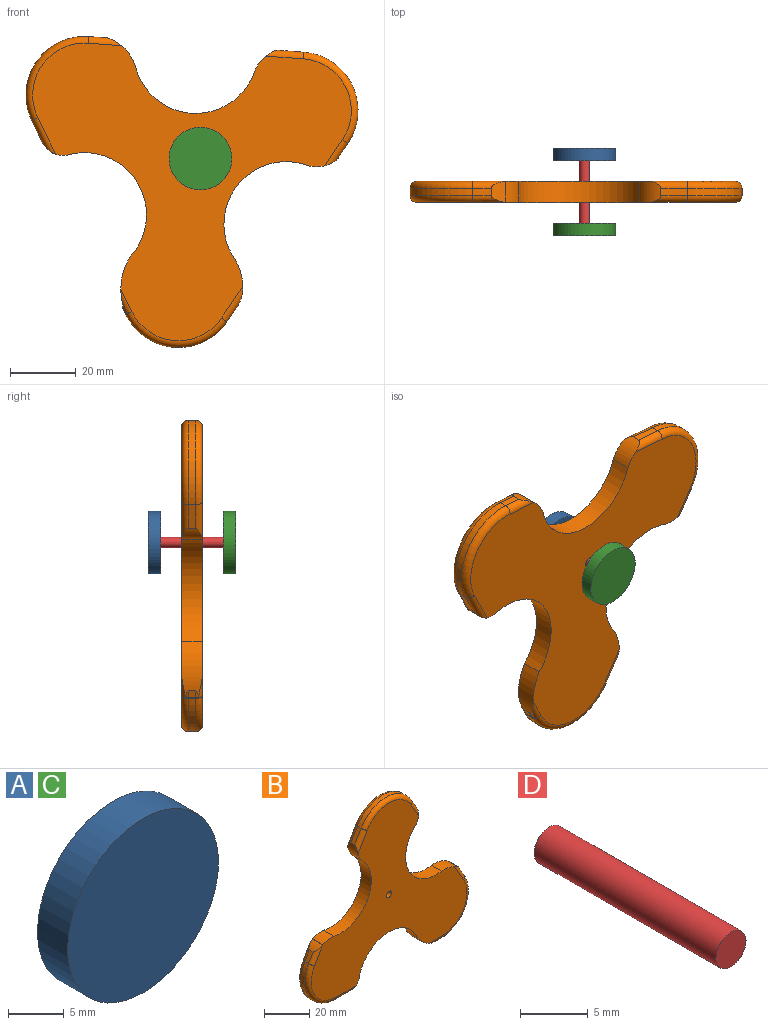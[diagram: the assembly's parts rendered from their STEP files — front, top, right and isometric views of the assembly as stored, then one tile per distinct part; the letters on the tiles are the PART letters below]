
ASSEMBLY  parts=4 mates=3
PART A: 3 faces, bbox 19.1x3.8x19.1 mm
  f0: cylinder r=9.53mm len=19.05mm, axis (0,1,0), area 228mm2, adj f1,f2
  f1: plane 19.05x19.05mm, normal (0,-1,0), area 285mm2, adj f0
  f2: plane 19.05x19.05mm, normal (0,1,0), area 285mm2, adj f0
PART B: 44 faces, bbox 105x7.5x96.3 mm
  f0: cylinder r=2.03mm len=9.3mm, axis (-0.5,0,0.87), area 23.9mm2, adj f2,f3,f8,f32,f43
  f1: cylinder r=2.03mm len=9.3mm, axis (0.5,0,-0.87), area 23.9mm2, adj f2,f3,f7,f28,f43
  f2: plane 4.6x2.66mm, normal (0.87,0,0.5), area 12.1mm2, adj f0,f1,f24,f43
  f3: cylinder r=10.84mm len=6.35mm, axis (0,-1,0), area 39.9mm2, adj f0,f1,f7,f8,f9,f43
  f4: cylinder r=2.03mm len=11.04mm, axis (0.5,0,-0.87), area 28.3mm2, adj f6,f7,f29,f41,f42
  f5: cylinder r=2.03mm len=11.04mm, axis (-0.5,0,0.87), area 28.3mm2, adj f6,f8,f31,f41,f42
  f6: plane 5.16x2.98mm, normal (0.87,0,0.5), area 13.6mm2, adj f4,f5,f26,f42
  f7: plane 96.9x88.14mm, normal (0,-1,0), area 4006.4mm2, adj f1,f3,f4,f9,f11,f13,f15,f18
  f8: plane 96.9x88.14mm, normal (0,1,0), area 4006.4mm2, adj f0,f3,f5,f9,f10,f13,f16,f17
  f9: cylinder r=18.98mm len=33.01mm, axis (0,-1,0), area 310.6mm2, adj f3,f7,f8,f41
  f10: cylinder r=2.03mm len=9.74mm, axis (-0.5,0,-0.87), area 25mm2, adj f8,f12,f33,f39
  f11: cylinder r=2.03mm len=9.74mm, axis (0.5,0,0.87), area 25mm2, adj f7,f12,f30,f39
  f12: plane 4.85x2.8mm, normal (-0.87,0,0.5), area 12.8mm2, adj f10,f11,f25,f39
  f13: cylinder r=13.28mm len=6.92mm, axis (0,-1,0), area 45.1mm2, adj f7,f8,f21,f40
  f14: plane 7.1x4.1mm, normal (-0.87,0,0.5), area 18.7mm2, adj f15,f16,f24,f38
  f15: cylinder r=2.03mm len=10.87mm, axis (0.5,0,0.87), area 31.2mm2, adj f7,f14,f28,f38
  f16: cylinder r=2.03mm len=10.87mm, axis (-0.5,0,-0.87), area 31.2mm2, adj f8,f14,f32,f38
  f17: cylinder r=2.03mm len=7.6mm, axis (1,0,0), area 10.3mm2, adj f8,f23,f31,f36,f37
  f18: cylinder r=2.03mm len=7.6mm, axis (-1,0,0), area 10.3mm2, adj f7,f23,f29,f36,f37
  f19: cylinder r=2.03mm len=12.33mm, axis (-1,0,0), area 32.5mm2, adj f7,f22,f30,f35
  f20: cylinder r=2.03mm len=12.33mm, axis (1,0,0), area 32.5mm2, adj f8,f22,f33,f35
  f21: cylinder r=18.92mm len=32.63mm, axis (0,-1,0), area 314.1mm2, adj f7,f8,f13,f38
  f22: plane 8.06x2.3mm, normal (0,0,-1), area 18.4mm2, adj f19,f20,f25,f35
  f23: plane 2.54x2.29mm, normal (0,0,-1), area 5.8mm2, adj f17,f18,f26,f37
  f24: cylinder r=17.78mm len=30.8mm, axis (0,1,0), area 85.1mm2, adj f2,f14,f28,f32
  f25: cylinder r=17.78mm len=26.67mm, axis (0,1,0), area 85.1mm2, adj f12,f22,f30,f33
  f26: cylinder r=17.78mm len=26.67mm, axis (0,1,0), area 85.1mm2, adj f6,f23,f29,f31
  f27: cylinder r=1.59mm len=6.35mm, axis (0,-1,0), area 63.3mm2, adj f7,f8
  f28: torus R=15.75mm, axis (0,-1,0), area 113.9mm2, adj f1,f7,f15,f24
  f29: torus R=15.75mm, axis (0,-1,0), area 113.9mm2, adj f4,f7,f18,f26
  f30: torus R=15.75mm, axis (0,-1,0), area 113.9mm2, adj f7,f11,f19,f25
  f31: torus R=15.75mm, axis (0,-1,0), area 113.9mm2, adj f5,f8,f17,f26
  f32: torus R=15.75mm, axis (0,-1,0), area 113.9mm2, adj f0,f8,f16,f24
  f33: torus R=15.75mm, axis (0,-1,0), area 113.9mm2, adj f8,f10,f20,f25
  f34: cylinder r=18.9mm len=36.31mm, axis (0,-1,0), area 314.3mm2, adj f7,f8,f35,f36
  f35: cylinder r=7.09mm len=6.35mm, axis (0,-1,0), area 44.9mm2, adj f7,f8,f19,f20,f22,f34
  f36: cylinder r=18.52mm len=14.82mm, axis (0,-1,0), area 103.6mm2, adj f7,f8,f17,f18,f34,f37
  f37: plane 5.14x3.42mm, normal (-0.08,0,1), area 7.9mm2, adj f17,f18,f23,f36
  f38: cylinder r=10.99mm len=8.53mm, axis (0,-1,0), area 50.5mm2, adj f7,f8,f14,f15,f16,f21
  f39: cylinder r=13.65mm len=6.35mm, axis (0,-1,0), area 21.3mm2, adj f10,f11,f12,f40
  f40: plane 6.35x0.05mm, normal (-0.87,0,0.5), area 0.4mm2, adj f7,f8,f13,f39
  f41: cylinder r=16.11mm len=9.81mm, axis (0,-1,0), area 64.7mm2, adj f4,f5,f7,f8,f9,f42
  f42: cylinder r=10.35mm len=5.71mm, axis (0,-1,0), area 15.8mm2, adj f4,f5,f6,f41
  f43: cylinder r=7.1mm len=5.73mm, axis (0,-1,0), area 12.2mm2, adj f0,f1,f2,f3
PART C: same geometry as A
PART D: 3 faces, bbox 3.1x19.1x3.1 mm
  f0: cylinder r=1.57mm len=19.05mm, axis (0,1,0), area 188.5mm2, adj f1,f2
  f1: plane 3.15x3.15mm, normal (0,-1,0), area 7.8mm2, adj f0
  f2: plane 3.15x3.15mm, normal (0,1,0), area 7.8mm2, adj f0
PLACE A t=(-34.86,14.65,11.48)mm
PLACE B rot(axis=(0,1,0),64.1deg) t=(-34.86,4.49,11.48)mm
PLACE C t=(-34.86,-8.21,11.48)mm
PLACE D t=(-34.86,10.84,11.48)mm fixed
MATE revolute B.f27 <-> D.f0  axis (0,-1,0) through (-34.86,1.32,11.48)mm
MATE fastened A.f0 <-> D.f0  axis (0,-1,0) through (-34.86,10.84,11.48)mm
MATE fastened C.f0 <-> D.f0  axis (0,1,0) through (-34.86,-8.21,11.48)mm
